# Revit family: LAMP_FIL 35 1680MM D-I OPAL
name_source: partatom
category: Luminarias
revit_build: Autodesk Revit 2018 (Build: 20190510_1515(x64)
units: mm (PartAtom-declared; Revit-internal decimal feet)

## family parameters
Anfitrión = Cara
Compartido = No
Corte con vacíos al cargar = No
Cota de conector redondo = Diámetro de uso
Origen de luz = Sí
Punto de cálculo de habitación = No
Tipo de pieza = Normal

## types (12) — shared parameters
CRI = 80
Cambio de temperatura de color de luz atenuada = <Ninguno>
Dimensions = 1680x35x80
Elevación por defecto = 1219 mm
Fabricante = LAMP
Filtro de color = 16777215
Gear = Electronic
IEE = A+
Installation instructions = https://www.lamp.es
Insulation class = I
LED Lifetime = 50.000 L90 B10
Lamp = MID-POWER LED
Last update = 14/05/2021
Longitud de línea de emisión = 840 mm  [stored 2.75591 ft]
MacAdam = 3
Manufacturer URL = http://www.lamp.es
Manufacturer country = Spain
Manufacturer name = LAMP
Material difusor = LAMP_PC Difusor Opal Fil
Material suspension = LAMP_Acero genérico
Plum = 32 W
Power = 27 W
Power Supply = 220-240V 50/60Hz
Product URL = https://www.lamp.es
Product datasheet = http://www.lamp.es
Protection rating = IP20 / IK07
Type = MID POWER TRIDONIC
Weight = 3.65 kg
Ángulo de inclinación = -90.00°

## per-type parameters (varying)
| type | Archivo de red fotométrica | Descripción | Efficacy | Finish | Indirect light | Material perfil | Modelo | Product code |
| 3388LM 3000K DALI BLACK | F31SF168LOIO830NB_D.IES | FIL35 SUR 1680 2400 WW D/I OPAL DALI BK. | 105 lm/W | Matte black RAL 9011 | LAMP_FIL 35 1680MM D-I OPAL_I : 3000K | LAMP_Aluminio Perfil Fil NG | F31SF168LOIO830DB | F31SF168LOIO830DB |
| 3388LM 3000K DALI GREY | F31SF168LOIO830NB_D.IES | FIL35 SUR 1680 2400 WW D/I OPAL DALI GR. | 105 lm/W | Gloss grey | LAMP_FIL 35 1680MM D-I OPAL_I : 3000K | LAMP_Aluminio Perfil Fil GR | F31SF168LOIO830DG | F31SF168LOIO830DG |
| 3388LM 3000K DALI WHITE | F31SF168LOIO830NB_D.IES | FIL35 SUR 1680 2400 WW D/I OPAL DALI WH. | 105 lm/W | Matte white RAL 9010 | LAMP_FIL 35 1680MM D-I OPAL_I : 3000K | LAMP_Aluminio Perfil Fil BL | F31SF168LOIO830DW | F31SF168LOIO830DW |
| 3388LM 3000K  BLACK | F31SF168LOIO830NB_D.IES | FIL35 SUR 1680 2400 WW D/I OPAL BK. | 105 lm/W | Matte black RAL 9011 | LAMP_FIL 35 1680MM D-I OPAL_I : 3000K | LAMP_Aluminio Perfil Fil NG | F31SF168LOIO830NB | F31SF168LOIO830NB |
| 3388LM 3000K  GREY | F31SF168LOIO830NB_D.IES | FIL35 SUR 1680 2400 WW D/I OPAL GR. | 105 lm/W | Gloss grey | LAMP_FIL 35 1680MM D-I OPAL_I : 3000K | LAMP_Aluminio Perfil Fil GR | F31SF168LOIO830NG | F31SF168LOIO830NG |
| 3388LM 3000K  WHITE | F31SF168LOIO830NB_D.IES | FIL35 SUR 1680 2400 WW D/I OPAL WH. | 105 lm/W | Matte white RAL 9010 | LAMP_FIL 35 1680MM D-I OPAL_I : 3000K | LAMP_Aluminio Perfil Fil BL | F31SF168LOIO830NW | F31SF168LOIO830NW |
| 3569LM 4000K DALI BLACK | F31SF168LOIO840NB_D.IES | FIL35 SUR 1680 2400 NW D/I OPAL DALI BK. | 111 lm/W | Matte black RAL 9011 | LAMP_FIL 35 1680MM D-I OPAL_I : 4000K | LAMP_Aluminio Perfil Fil NG | F31SF168LOIO840DB | F31SF168LOIO840DB |
| 3569LM 4000K DALI GREY | F31SF168LOIO840NB_D.IES | FIL35 SUR 1680 2400 NW D/I OPAL DALI GR. | 111 lm/W | Gloss grey | LAMP_FIL 35 1680MM D-I OPAL_I : 4000K | LAMP_Aluminio Perfil Fil GR | F31SF168LOIO840DG | F31SF168LOIO840DG |
| 3569LM 4000K DALI WHITE | F31SF168LOIO840NB_D.IES | FIL35 SUR 1680 2400 NW D/I OPAL DALI WH. | 111 lm/W | Matte white RAL 9010 | LAMP_FIL 35 1680MM D-I OPAL_I : 4000K | LAMP_Aluminio Perfil Fil BL | F31SF168LOIO840DW | F31SF168LOIO840DW |
| 3569LM 4000K  BLACK | F31SF168LOIO840NB_D.IES | FIL35 SUR 1680 2400 NW D/I OPAL BK. | 111 lm/W | Matte black RAL 9011 | LAMP_FIL 35 1680MM D-I OPAL_I : 4000K | LAMP_Aluminio Perfil Fil NG | F31SF168LOIO840NB | F31SF168LOIO840NB |
| 3569LM 4000K  GREY | F31SF168LOIO840NB_D.IES | FIL35 SUR 1680 2400 NW D/I OPAL GR. | 111 lm/W | Gloss grey | LAMP_FIL 35 1680MM D-I OPAL_I : 4000K | LAMP_Aluminio Perfil Fil GR | F31SF168LOIO840NG | F31SF168LOIO840NG |
| 3569LM 4000K  WHITE | F31SF168LOIO840NB_D.IES | FIL35 SUR 1680 2400 NW D/I OPAL WH. | 111 lm/W | Matte white RAL 9010 | LAMP_FIL 35 1680MM D-I OPAL_I : 4000K | LAMP_Aluminio Perfil Fil BL | F31SF168LOIO840NW | F31SF168LOIO840NW |

note: [stored X ft] marks values corroborated as IEEE doubles in the binary element streams (Revit-internal decimal feet)
